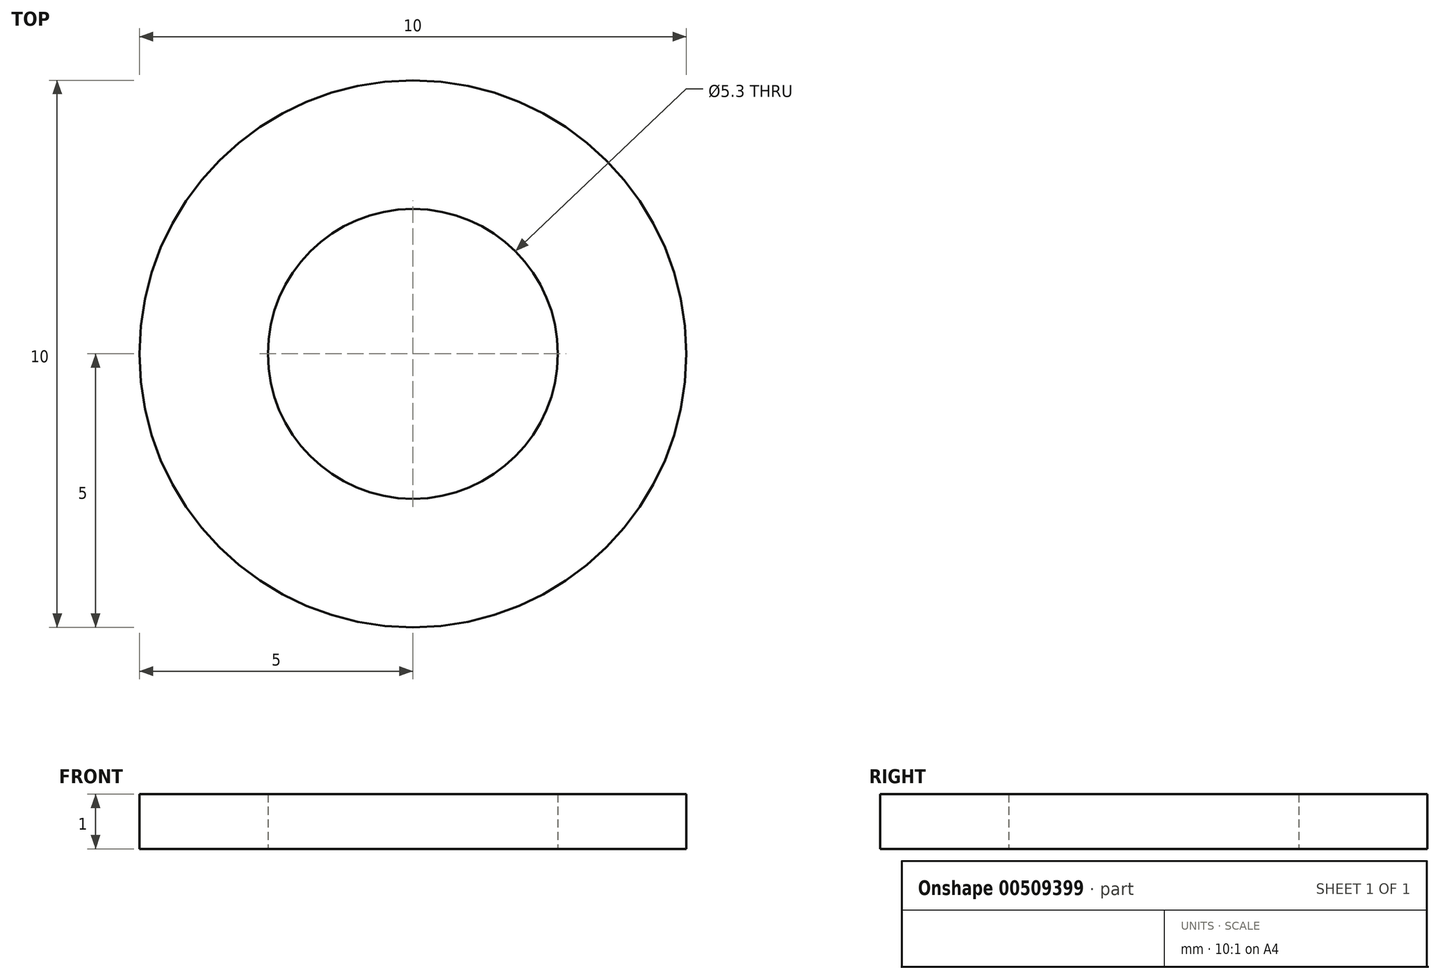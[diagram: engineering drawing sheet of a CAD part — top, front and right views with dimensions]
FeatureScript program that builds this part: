
annotation { "Feature Type Name" : "Feature", "Feature Type Description" : "" }
export const myFeature = defineFeature(function(context is Context, id is Id, definition is map)
    precondition{}
    {
        {
            var Q0;
            Q0=qCreatedBy(makeId("Top.planeOp"),FACE);
            var sketch = newSketch(context, id + "F0", { "sketchPlane" : qUnion([Q0])});
            skCircle(sketch, "E0", {"center": v(0, 0) * mm, "radius": 5 * mm});
            skCircle(sketch, "E1", {"center": v(0, 0) * mm, "radius": 2.65 * mm});
            skSolve(sketch);
        }
        {
            var Q0;
            Q0=qSketchRegion(id+"F0",true);
            extrude(context, id + "F1", {"entities" : qUnion([Q0]), "depth" : 1 * mm});
        }
    });
